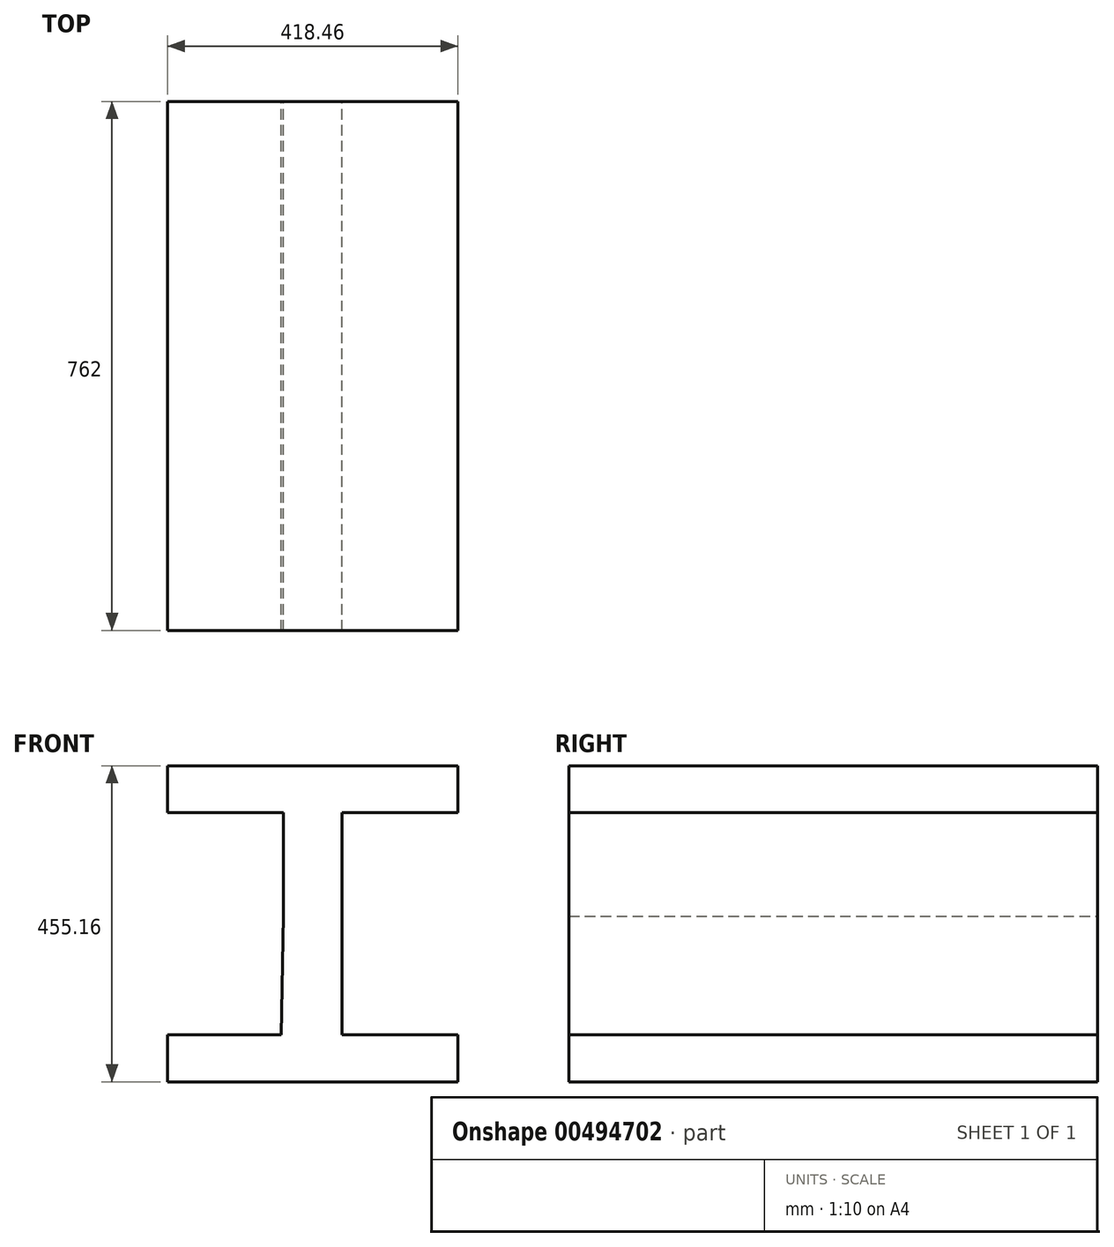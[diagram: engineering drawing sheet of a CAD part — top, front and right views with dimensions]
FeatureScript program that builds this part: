
annotation { "Feature Type Name" : "Feature", "Feature Type Description" : "" }
export const myFeature = defineFeature(function(context is Context, id is Id, definition is map)
    precondition{}
    {
        {
            var Q0;
            Q0=qCreatedBy(makeId("Front.planeOp"),FACE);
            var sketch = newSketch(context, id + "F0", { "sketchPlane" : qUnion([Q0])});
            skLineSegment(sketch, "E0", {"start": v(-42.04, 0) * mm, "end": v(-42.04, 149.34) * mm});
            skLineSegment(sketch, "E1", {"start": v(-42.04, 149.34) * mm, "end": v(-209.23, 149.34) * mm});
            skLineSegment(sketch, "E2", {"start": v(-209.23, 149.34) * mm, "end": v(-209.23, 216.9) * mm});
            skLineSegment(sketch, "E3", {"start": v(-209.23, 216.9) * mm, "end": v(209.23, 216.9) * mm});
            skLineSegment(sketch, "E4", {"start": v(209.23, 216.9) * mm, "end": v(209.23, 149.34) * mm});
            skLineSegment(sketch, "E5", {"start": v(209.23, 149.34) * mm, "end": v(42.04, 149.34) * mm});
            skLineSegment(sketch, "E6", {"start": v(42.04, 149.34) * mm, "end": v(42.04, 0) * mm});
            skLineSegment(sketch, "E7", {"start": v(42.04, 0) * mm, "end": v(42.04, -170.7) * mm});
            skLineSegment(sketch, "E8", {"start": v(42.04, -170.7) * mm, "end": v(209.23, -170.7) * mm});
            skLineSegment(sketch, "E9", {"start": v(209.23, -170.7) * mm, "end": v(209.23, -238.26) * mm});
            skLineSegment(sketch, "E10", {"start": v(209.23, -238.26) * mm, "end": v(-209.23, -238.26) * mm});
            skLineSegment(sketch, "E11", {"start": v(-209.23, -238.26) * mm, "end": v(-209.23, -170.7) * mm});
            skLineSegment(sketch, "E12", {"start": v(-209.23, -170.7) * mm, "end": v(-45.42, -170.7) * mm});
            skLineSegment(sketch, "E13", {"start": v(-45.42, -170.7) * mm, "end": v(-42.04, 0) * mm});
            skSolve(sketch);
        }
        {
            var Q0;
            Q0 = qSketchRegion(id + "F0", true);
            extrude(context, id + "F1", {"entities" : qUnion([Q0]), "depth" : 762 * mm});
        }
    });
